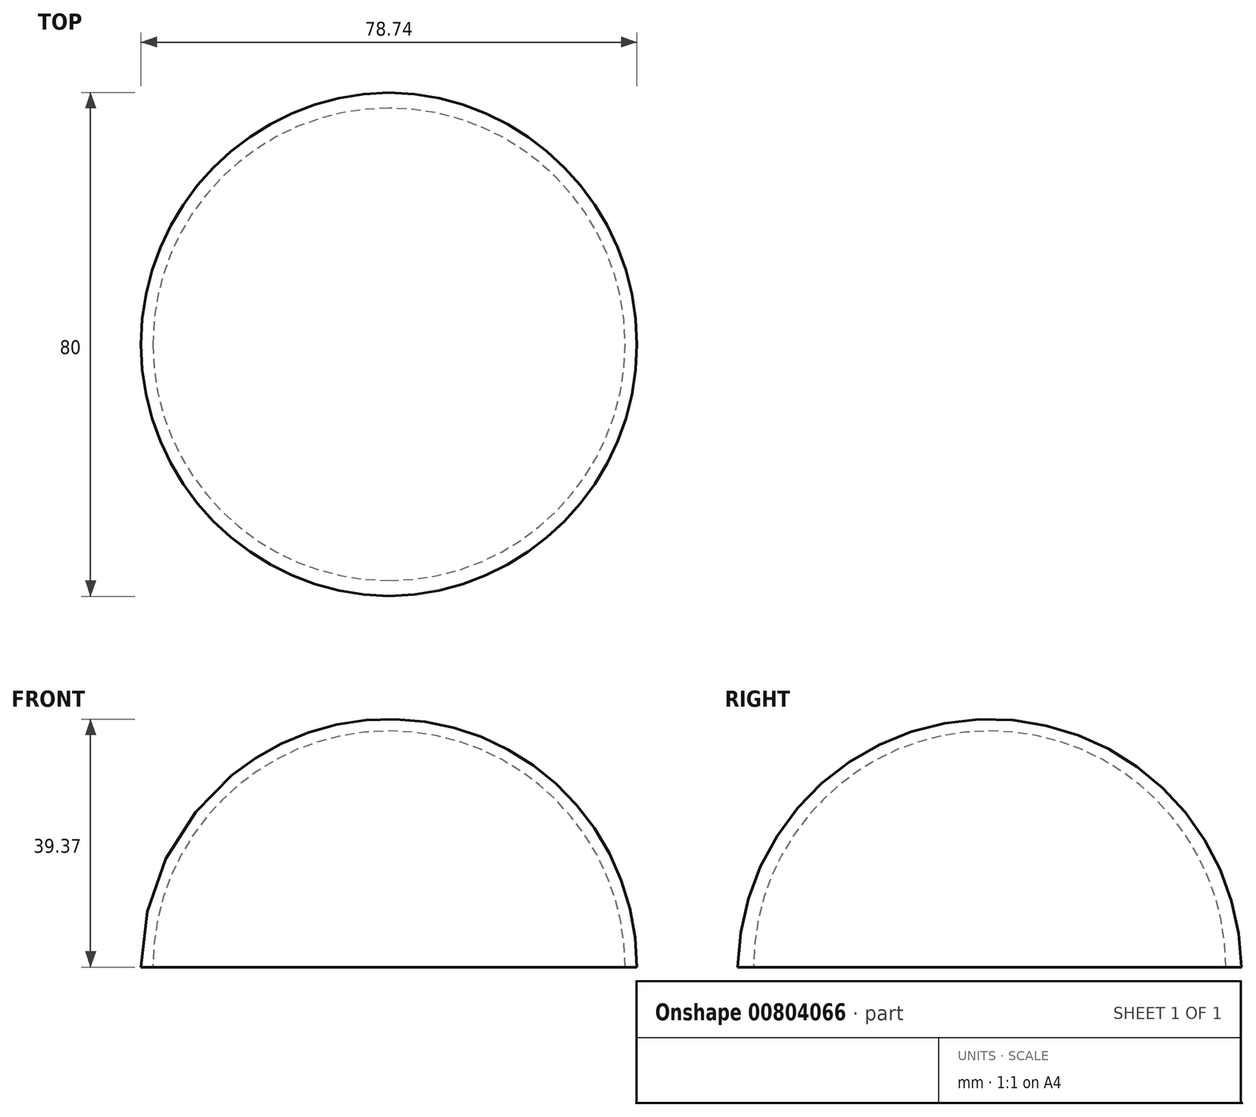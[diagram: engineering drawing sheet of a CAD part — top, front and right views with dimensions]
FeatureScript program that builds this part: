
annotation { "Feature Type Name" : "Feature", "Feature Type Description" : "" }
export const myFeature = defineFeature(function(context is Context, id is Id, definition is map)
    precondition{}
    {
        {
            var Q0;
            Q0=qCreatedBy(makeId("Top.planeOp"),FACE);
            var sketch = newSketch(context, id + "F0", { "sketchPlane" : qUnion([Q0])});
            skArc(sketch, "E0", {"start": v(0, -40) * mm, "mid": v(39.37, 0) * mm, "end": v(0, 40) * mm});
            skLineSegment(sketch, "E1", {"start": v(0, 40) * mm, "end": v(0, -40) * mm});
            skLineSegment(sketch, "E2", {"start": v(0, -40) * mm, "end": v(-38.14, -40.6) * mm, "construction": true});
            skLineSegment(sketch, "E3", {"start": v(0, 40) * mm, "end": v(-45.92, 40.71) * mm, "construction": true});
            skSolve(sketch);
        }
        {
            var Q0;
            Q0=qSketchRegion(id+"F0",true);
            var Q1;
            Q1=sQuery(id+"F0.wireOp",EDGE,"E1");
            revolve(context, id + "F1", {"surfaceOperationType" : NewSurfaceOperationType.NEW, "entities" : qUnion([Q0]), "axis" : qUnion([Q1]), "revolveType" : RevolveType.ONE_DIRECTION, "angle" : 180 * degree});
        }
        {
            var Q0;
            Q0=makeQuery(id+"F1.opRevolve","CAP_FACE",FACE,{"disambiguationData":[OSD([sQuery(id+"F0.wireOp",EDGE,"E0"),sQuery(id+"F0.wireOp",EDGE,"E1")])],"isStart":false});
            var sketch = newSketch(context, id + "F2", { "sketchPlane" : qUnion([Q0])});
            skArc(sketch, "E4", {"start": v(0, 37.5) * mm, "mid": v(-37.5, 0) * mm, "end": v(0, -37.5) * mm});
            skLineSegment(sketch, "E5", {"start": v(0, 37.5) * mm, "end": v(0, -37.5) * mm});
            skSolve(sketch);
        }
        {
            var Q0;
            Q0 = qSketchRegion(id + "F2", true);
            var Q1;
            Q1=sQuery(id+"F2.wireOp",EDGE,"E5");
            revolve(context, id + "F3", {"operationType" : NewBodyOperationType.REMOVE, "surfaceOperationType" : NewSurfaceOperationType.NEW, "entities" : qUnion([Q0]), "axis" : qUnion([Q1]), "revolveType" : RevolveType.FULL, "oppositeDirection" : true});
        }
    });
